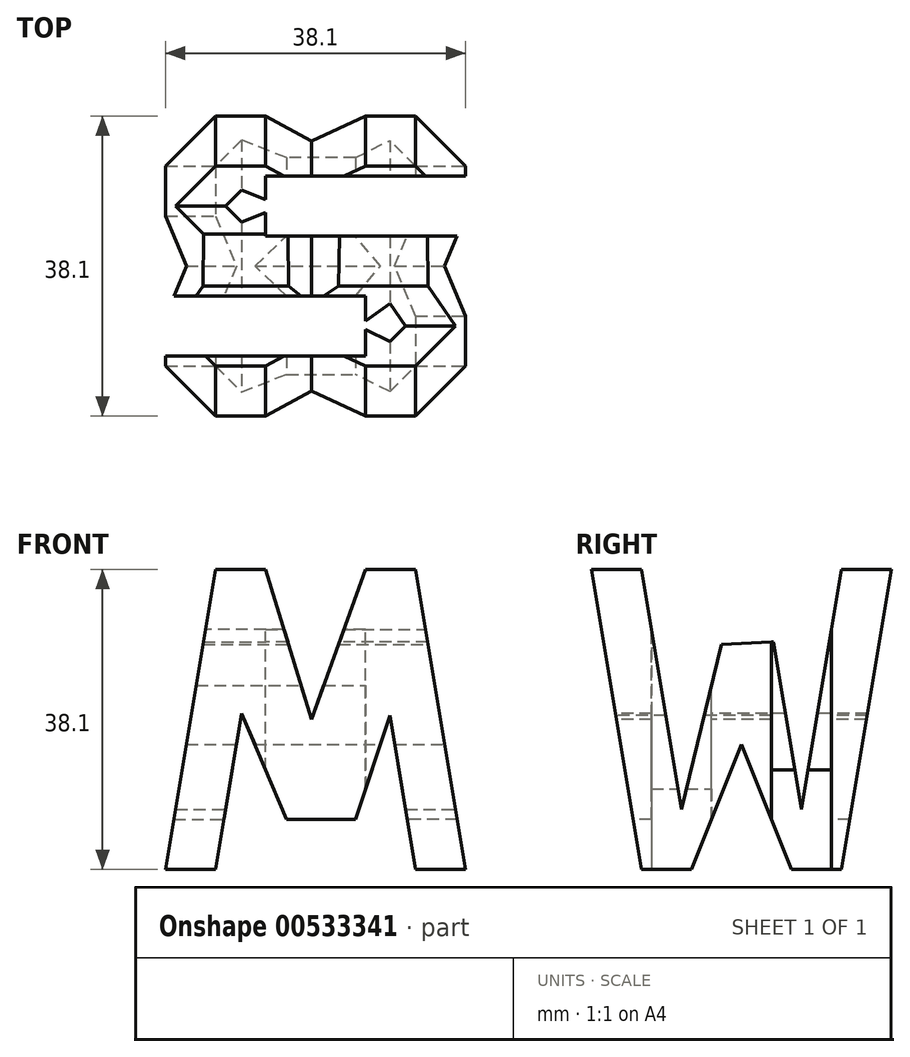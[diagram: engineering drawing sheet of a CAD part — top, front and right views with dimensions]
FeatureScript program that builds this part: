
annotation { "Feature Type Name" : "Feature", "Feature Type Description" : "" }
export const myFeature = defineFeature(function(context is Context, id is Id, definition is map)
    precondition{}
    {
        {
            var Q0;
            Q0=qCreatedBy(makeId("Front.planeOp"),FACE);
            var sketch = newSketch(context, id + "F0", { "sketchPlane" : qUnion([Q0])});
            skLineSegment(sketch, "E0", {"start": v(0, 0) * mm, "end": v(38.1, 0) * mm});
            skLineSegment(sketch, "E1", {"start": v(0, 0) * mm, "end": v(0, 38.1) * mm});
            skLineSegment(sketch, "E2", {"start": v(0, 38.1) * mm, "end": v(38.1, 38.1) * mm});
            skLineSegment(sketch, "E3", {"start": v(38.1, 38.1) * mm, "end": v(38.1, 0) * mm});
            skSolve(sketch);
        }
        {
            var Q0;
            Q0 = qSketchRegion(id + "F0", true);
            extrude(context, id + "F1", {"entities" : qUnion([Q0]), "depth" : 38.1 * mm, "offsetDistance" : 25.4 * mm});
        }
        {
            var Q0;
            Q0=qCreatedBy(makeId("Front.planeOp"),FACE);
            cPlane(context, id + "F2", {"entities" : qUnion([Q0]), "cplaneType" : CPlaneType.OFFSET, "offset" : 38.1 * mm, "width" : 152.4 * mm, "height" : 152.4 * mm});
        }
        {
            var Q0;
            Q0=qCreatedBy(makeId("Right.planeOp"),FACE);
            cPlane(context, id + "F3", {"entities" : qUnion([Q0]), "cplaneType" : CPlaneType.OFFSET, "offset" : 38.1 * mm, "width" : 152.4 * mm, "height" : 152.4 * mm});
        }
        {
            var Q0;
            Q0=qCreatedBy(makeId("Top.planeOp"),FACE);
            cPlane(context, id + "F4", {"entities" : qUnion([Q0]), "cplaneType" : CPlaneType.OFFSET, "offset" : 38.1 * mm, "width" : 152.4 * mm, "height" : 152.4 * mm});
        }
        {
            var Q0;
            Q0=qCreatedBy(id+"F3.planeOp",FACE);
            var sketch = newSketch(context, id + "F5", { "sketchPlane" : qUnion([Q0])});
            skLineSegment(sketch, "E4", {"start": v(0, 0) * mm, "end": v(0, 38.1) * mm});
            skLineSegment(sketch, "E5", {"start": v(0, 38.1) * mm, "end": v(-38.1, 38.1) * mm});
            skLineSegment(sketch, "E6", {"start": v(-38.1, 38.1) * mm, "end": v(-38.1, 0) * mm});
            skLineSegment(sketch, "E7", {"start": v(-38.1, 0) * mm, "end": v(0, 0) * mm});
            skLineSegment(sketch, "E8", {"start": v(-38.1, 38.1) * mm, "end": v(-31.75, 0) * mm});
            skLineSegment(sketch, "E9", {"start": v(-25.4, 0) * mm, "end": v(-19.05, 15.88) * mm});
            skLineSegment(sketch, "E10", {"start": v(-19.05, 15.88) * mm, "end": v(-12.7, 0) * mm});
            skLineSegment(sketch, "E11", {"start": v(-6.35, 0) * mm, "end": v(0, 38.1) * mm});
            skLineSegment(sketch, "E12", {"start": v(-31.75, 38.1) * mm, "end": v(-26.67, 7.64) * mm});
            skLineSegment(sketch, "E13", {"start": v(-26.67, 7.64) * mm, "end": v(-21.6, 28.58) * mm});
            skLineSegment(sketch, "E14", {"start": v(-11.43, 7.64) * mm, "end": v(-6.35, 38.1) * mm});
            skPoint(sketch, "E15.start.orphan", {"position": v(-21.59, 14.55) * mm});
            skPoint(sketch, "E16.start.orphan", {"position": v(-16.5, 14.55) * mm});
            skLineSegment(sketch, "E17", {"start": v(-11.43, 7.64) * mm, "end": v(-14.97, 28.89) * mm});
            skLineSegment(sketch, "E18", {"start": v(-21.6, 28.58) * mm, "end": v(-14.97, 28.89) * mm});
            skSolve(sketch);
        }
        {
            var Q0;
            {var subQ1=sQuery(id+"F5.wireOp",EDGE,"E12");Q0=makeQuery(id+"F5.imprint","IMPRINT",FACE,{"disambiguationData":[TD([[makeQuery(id+"F5.imprint","IMPRINT",EDGE,{"derivedFrom":subQ1}),1.0]])]});}
            var Q1;
            {var subQ0=sQuery(id+"F5.wireOp",EDGE,"E6");Q1=makeQuery(id+"F5.imprint","IMPRINT",FACE,{"disambiguationData":[TD([[makeQuery(id+"F5.imprint","IMPRINT",EDGE,{"derivedFrom":subQ0}),1.0]])]});}
            var Q2;
            {var subQ0=sQuery(id+"F5.wireOp",EDGE,"E9");Q2=makeQuery(id+"F5.imprint","IMPRINT",FACE,{"disambiguationData":[TD([[makeQuery(id+"F5.imprint","IMPRINT",EDGE,{"derivedFrom":subQ0}),-1.0]])]});}
            var Q3;
            {var subQ0=sQuery(id+"F5.wireOp",EDGE,"E4");Q3=makeQuery(id+"F5.imprint","IMPRINT",FACE,{"disambiguationData":[TD([[makeQuery(id+"F5.imprint","IMPRINT",EDGE,{"derivedFrom":subQ0}),1.0]])]});}
            extrude(context, id + "F6", {"entities" : qUnion([Q0, Q1, Q2, Q3]), "operationType" : NewBodyOperationType.REMOVE, "oppositeDirection" : true, "depth" : 38.1 * mm, "offsetDistance" : 25.4 * mm});
        }
        {
            var Q0;
            Q0=qCreatedBy(id+"F2.planeOp",FACE);
            var sketch = newSketch(context, id + "F7", { "sketchPlane" : qUnion([Q0])});
            skLineSegment(sketch, "E19.bottom", {"start": v(0, 0) * mm, "end": v(38.1, 0) * mm});
            skLineSegment(sketch, "E19.top", {"start": v(0, 38.1) * mm, "end": v(38.1, 38.1) * mm});
            skLineSegment(sketch, "E19.left", {"start": v(0, 0) * mm, "end": v(0, 38.1) * mm});
            skLineSegment(sketch, "E19.right", {"start": v(38.1, 0) * mm, "end": v(38.1, 38.1) * mm});
            skLineSegment(sketch, "E20", {"start": v(0, 0) * mm, "end": v(6.35, 38.1) * mm});
            skLineSegment(sketch, "E21", {"start": v(38.1, 0) * mm, "end": v(31.75, 38.1) * mm});
            skLineSegment(sketch, "E22", {"start": v(18.54, 19.05) * mm, "end": v(25.4, 38.1) * mm});
            skPoint(sketch, "E22.startSnap0", {"position": v(3.17, 19.05) * mm});
            skLineSegment(sketch, "E23", {"start": v(18.54, 19.05) * mm, "end": v(12.7, 38.1) * mm});
            skLineSegment(sketch, "E24", {"start": v(6.35, 0) * mm, "end": v(9.66, 19.84) * mm});
            skLineSegment(sketch, "E25", {"start": v(16.5, 24.72) * mm, "end": v(16.8, 24.72) * mm});
            skLineSegment(sketch, "E26", {"start": v(28.5, 19.53) * mm, "end": v(31.75, 0) * mm});
            skPoint(sketch, "E27.start.orphan", {"position": v(11.43, 30.48) * mm});
            skLineSegment(sketch, "E28.trimOffspring", {"start": v(20.58, 24.72) * mm, "end": v(21.59, 24.72) * mm});
            skPoint(sketch, "E29.end.orphan", {"position": v(26.67, 30.48) * mm});
            skLineSegment(sketch, "E30", {"start": v(9.66, 19.84) * mm, "end": v(15.37, 6.35) * mm});
            skLineSegment(sketch, "E31", {"start": v(15.37, 6.35) * mm, "end": v(24.12, 6.35) * mm});
            skLineSegment(sketch, "E32", {"start": v(28.5, 19.53) * mm, "end": v(24.12, 6.35) * mm});
            skSolve(sketch);
        }
        {
            var Q0;
            {var subQ0=sQuery(id+"F7.wireOp",EDGE,"E19.left");Q0=makeQuery(id+"F7.imprint","IMPRINT",FACE,{"disambiguationData":[TD([[makeQuery(id+"F7.imprint","IMPRINT",EDGE,{"derivedFrom":subQ0}),-1.0]])]});}
            var Q1;
            {var subQ1=sQuery(id+"F7.wireOp",EDGE,"E22");var subQ6=makeQuery(id+"F7.imprint","IMPRINT",VERTEX,{"derivedFrom":subQ1});Q1=makeQuery(id+"F7.imprint","IMPRINT",FACE,{"disambiguationData":[TD([[makeQuery(id+"F7.imprint","IMPRINT",EDGE,{"disambiguationData":[TD([[subQ6,1.0]])],"derivedFrom":subQ1}),1.0]])]});}
            var Q2;
            {var subQ0=sQuery(id+"F7.wireOp",EDGE,"E19.right");Q2=makeQuery(id+"F7.imprint","IMPRINT",FACE,{"disambiguationData":[TD([[makeQuery(id+"F7.imprint","IMPRINT",EDGE,{"derivedFrom":subQ0}),1.0]])]});}
            var Q3;
            {var subQ1=sQuery(id+"F7.wireOp",EDGE,"E24");Q3=makeQuery(id+"F7.imprint","IMPRINT",FACE,{"disambiguationData":[TD([[makeQuery(id+"F7.imprint","IMPRINT",EDGE,{"derivedFrom":subQ1}),-1.0]])]});}
            extrude(context, id + "F8", {"entities" : qUnion([Q0, Q1, Q2, Q3]), "operationType" : NewBodyOperationType.REMOVE, "oppositeDirection" : true, "depth" : 38.1 * mm, "offsetDistance" : 25.4 * mm});
        }
        {
            var Q0;
            Q0=qCreatedBy(id+"F4.planeOp",FACE);
            var sketch = newSketch(context, id + "F9", { "sketchPlane" : qUnion([Q0])});
            skLineSegment(sketch, "E33", {"start": v(0, 0) * mm, "end": v(38.1, 0) * mm});
            skLineSegment(sketch, "E34", {"start": v(38.1, 0) * mm, "end": v(38.1, -38.1) * mm});
            skLineSegment(sketch, "E35", {"start": v(38.1, -38.1) * mm, "end": v(0, -38.1) * mm});
            skLineSegment(sketch, "E36", {"start": v(0, -38.1) * mm, "end": v(0, 0) * mm});
            skLineSegment(sketch, "E37", {"start": v(38.1, -7.62) * mm, "end": v(12.7, -7.62) * mm});
            skLineSegment(sketch, "E38", {"start": v(12.7, -7.62) * mm, "end": v(12.7, -15.24) * mm});
            skLineSegment(sketch, "E39", {"start": v(12.7, -15.24) * mm, "end": v(38.1, -15.24) * mm});
            skLineSegment(sketch, "E40", {"start": v(0, -30.48) * mm, "end": v(25.4, -30.48) * mm});
            skLineSegment(sketch, "E41", {"start": v(25.4, -30.48) * mm, "end": v(25.4, -22.86) * mm});
            skLineSegment(sketch, "E42", {"start": v(25.4, -22.86) * mm, "end": v(0, -22.86) * mm});
            skSolve(sketch);
        }
        {
            var Q0;
            {var subQ0=sQuery(id+"F9.wireOp",EDGE,"E37");Q0=makeQuery(id+"F9.imprint","IMPRINT",FACE,{"disambiguationData":[TD([[makeQuery(id+"F9.imprint","IMPRINT",EDGE,{"derivedFrom":subQ0}),1.0]])]});}
            var Q1;
            {var subQ0=sQuery(id+"F9.wireOp",EDGE,"E40");Q1=makeQuery(id+"F9.imprint","IMPRINT",FACE,{"disambiguationData":[TD([[makeQuery(id+"F9.imprint","IMPRINT",EDGE,{"derivedFrom":subQ0}),1.0]])]});}
            extrude(context, id + "F10", {"entities" : qUnion([Q0, Q1]), "operationType" : NewBodyOperationType.REMOVE, "oppositeDirection" : true, "depth" : 38.1 * mm, "offsetDistance" : 25.4 * mm});
        }
    });
